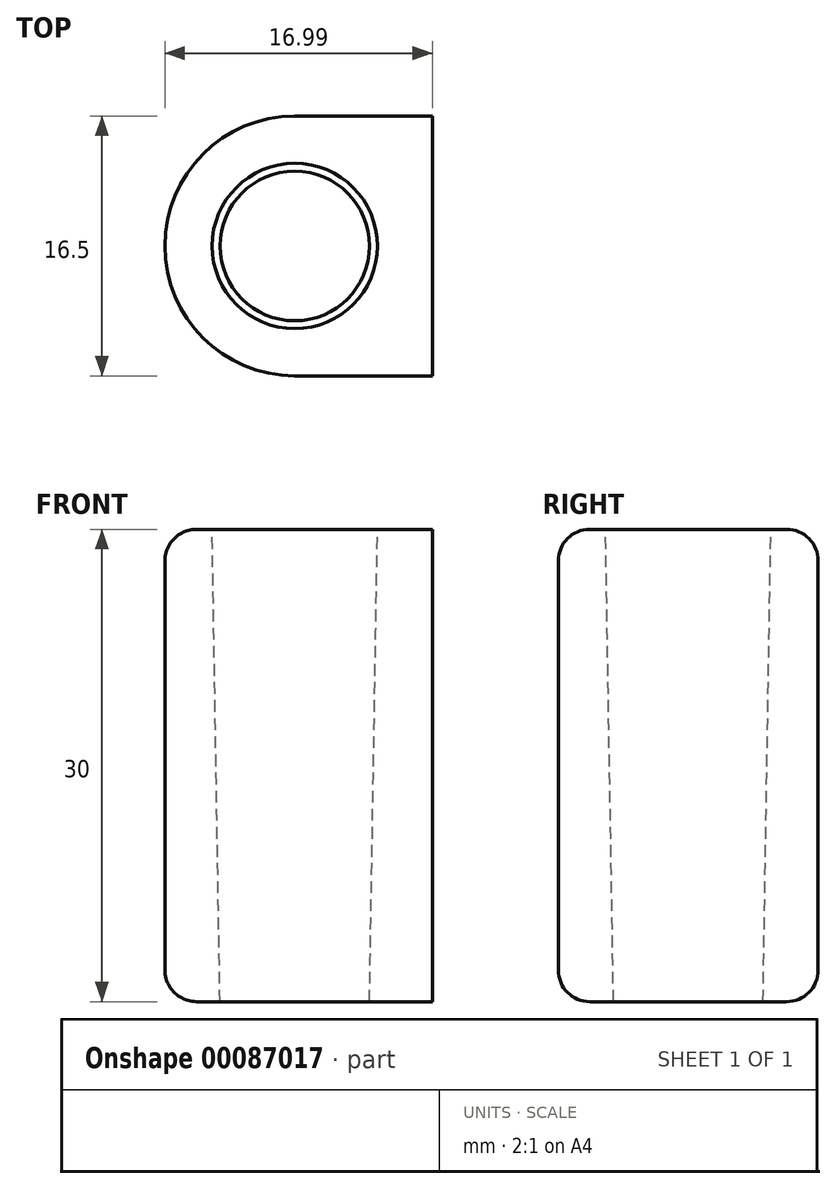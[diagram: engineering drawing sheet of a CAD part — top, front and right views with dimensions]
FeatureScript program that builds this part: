
annotation { "Feature Type Name" : "Feature", "Feature Type Description" : "" }
export const myFeature = defineFeature(function(context is Context, id is Id, definition is map)
    precondition{}
    {
        {
            var Q0;
            Q0=qCreatedBy(makeId("Front.planeOp"),FACE);
            var sketch = newSketch(context, id + "F0", { "sketchPlane" : qUnion([Q0])});
            skLineSegment(sketch, "E0", {"start": v(0, 52.01) * mm, "end": v(0, 22.01) * mm, "construction": true});
            skLineSegment(sketch, "E1", {"start": v(0, 52.01) * mm, "end": v(-5.25, 52.01) * mm, "construction": true});
            skLineSegment(sketch, "E2", {"start": v(0, 22.01) * mm, "end": v(-4.75, 22.01) * mm, "construction": true});
            skLineSegment(sketch, "E3", {"start": v(-5.25, 52.01) * mm, "end": v(-4.75, 22.01) * mm});
            skLineSegment(sketch, "E4", {"start": v(-5.25, 52.01) * mm, "end": v(-8.25, 52.01) * mm});
            skLineSegment(sketch, "E5", {"start": v(-8.25, 52.01) * mm, "end": v(-8.25, 22.01) * mm});
            skLineSegment(sketch, "E6", {"start": v(-8.25, 22.01) * mm, "end": v(-4.75, 22.01) * mm});
            skSolve(sketch);
        }
        {
            var Q0;
            Q0=makeQuery(id+"F0.imprint","IMPRINT",FACE,{"disambiguationData":[TD([[makeQuery(id+"F0.imprint","IMPRINT",EDGE,{"derivedFrom":sQuery(id+"F0.wireOp",EDGE,"E3")}),-1.0]])]});
            var Q1;
            Q1=sQuery(id+"F0.wireOp",EDGE,"E0");
            revolve(context, id + "F1", {"entities" : qUnion([Q0]), "axis" : qUnion([Q1]), "revolveType" : RevolveType.FULL});
        }
        {
            var Q0;
            Q0=makeQuery(id+"F1.opRevolve","SWEPT_FACE",FACE,{"disambiguationData":[OSD([sQuery(id+"F0.wireOp",EDGE,"E4")])]});
            var sketch = newSketch(context, id + "F2", { "sketchPlane" : qUnion([Q0])});
            skLineSegment(sketch, "E7.bottom", {"start": v(0, 8.25) * mm, "end": v(8.74, 8.25) * mm});
            skLineSegment(sketch, "E7.top", {"start": v(0, 5.55) * mm, "end": v(8.74, 5.55) * mm});
            skLineSegment(sketch, "E7.left", {"start": v(0, 8.25) * mm, "end": v(0, 5.55) * mm});
            skLineSegment(sketch, "E7.right", {"start": v(8.74, 8.25) * mm, "end": v(8.74, 5.55) * mm});
            skLineSegment(sketch, "E8.bottom", {"start": v(0, -8.25) * mm, "end": v(8.74, -8.25) * mm});
            skLineSegment(sketch, "E8.top", {"start": v(0, -5.64) * mm, "end": v(8.74, -5.64) * mm});
            skLineSegment(sketch, "E8.left", {"start": v(0, -8.25) * mm, "end": v(0, -5.64) * mm});
            skLineSegment(sketch, "E8.right", {"start": v(8.74, -8.25) * mm, "end": v(8.74, -5.64) * mm});
            skLineSegment(sketch, "E9.bottom", {"start": v(8.74, 8.25) * mm, "end": v(5.43, 8.25) * mm});
            skLineSegment(sketch, "E9.top", {"start": v(8.74, -8.25) * mm, "end": v(5.43, -8.25) * mm});
            skLineSegment(sketch, "E9.left", {"start": v(8.74, 8.25) * mm, "end": v(8.74, -8.25) * mm});
            skLineSegment(sketch, "E9.right", {"start": v(5.43, 8.25) * mm, "end": v(5.43, -8.25) * mm});
            skSolve(sketch);
        }
        {
            var Q0;
            Q0 = qSketchRegion(id + "F2", true);
            extrude(context, id + "F3", {"entities" : qUnion([Q0]), "operationType" : NewBodyOperationType.ADD, "oppositeDirection" : true, "depth" : 30 * mm});
        }
        {
            var Q0;
            Q0=makeQuery(id+"F3.opExtrude","SWEPT_EDGE",EDGE,{"disambiguationData":[OSD([sQuery(id+"F2.wireOp",EDGE,"E9.top"),sQuery(id+"F2.wireOp",EDGE,"E9.left")])]});
            var Q1;
            Q1=makeQuery(id+"F3.opExtrude","SWEPT_EDGE",EDGE,{"disambiguationData":[OSD([sQuery(id+"F2.wireOp",EDGE,"E9.bottom"),sQuery(id+"F2.wireOp",EDGE,"E9.left")])]});
            var Q2;
            Q2=makeQuery(id+"F3.opExtrude","CAP_EDGE",EDGE,{"disambiguationData":[OSD([sQuery(id+"F2.wireOp",EDGE,"E8.bottom"),sQuery(id+"F2.wireOp",EDGE,"E9.top")])],"isStart":true});
            var Q3;
            Q3=makeQuery(id+"F1.opRevolve","SWEPT_EDGE",EDGE,{"disambiguationData":[OSD([sQuery(id+"F0.wireOp",EDGE,"E5"),sQuery(id+"F0.wireOp",EDGE,"E6")])]});
            fillet(context, id + "F4", {"entities" : qUnion([Q0, Q1, Q2, Q3]), "radius" : 2 * mm, "tangentPropagation" : true, "allowEdgeOverflow" : false});
        }
    });
